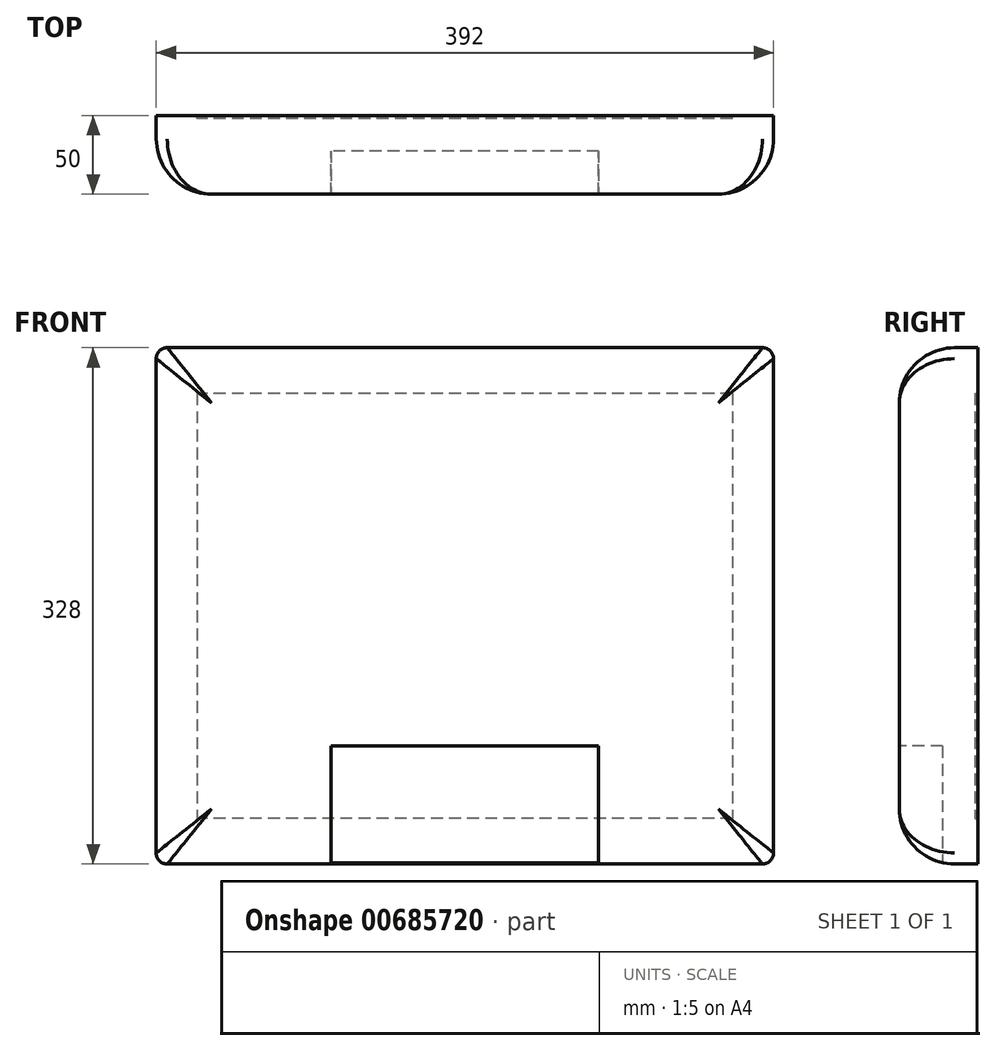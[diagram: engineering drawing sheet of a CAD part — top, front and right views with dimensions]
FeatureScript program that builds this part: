
annotation { "Feature Type Name" : "Feature", "Feature Type Description" : "" }
export const myFeature = defineFeature(function(context is Context, id is Id, definition is map)
    precondition{}
    {
        {
            var Q0;
            Q0=qCreatedBy(makeId("Front.planeOp"),FACE);
            var sketch = newSketch(context, id + "F0", { "sketchPlane" : qUnion([Q0])});
            skLineSegment(sketch, "E0.bottom", {"start": v(189, 164) * mm, "end": v(-189, 164) * mm});
            skLineSegment(sketch, "E0.top", {"start": v(189, -164) * mm, "end": v(-189, -164) * mm});
            skLineSegment(sketch, "E0.left", {"start": v(196, 157) * mm, "end": v(196, -157) * mm});
            skLineSegment(sketch, "E0.right", {"start": v(-196, 157) * mm, "end": v(-196, -157) * mm});
            skPoint(sketch, "E0.middle", {"position": v(0, 0) * mm});
            skPoint(sketch, "E1.visualSharp", {"position": v(-196, 164) * mm});
            skArc(sketch, "E1.filletArc", {"start": v(-189, 164) * mm, "mid": v(-193.95, 161.95) * mm, "end": v(-196, 157) * mm});
            skPoint(sketch, "E2.visualSharp", {"position": v(196, 164) * mm});
            skArc(sketch, "E2.filletArc", {"start": v(196, 157) * mm, "mid": v(193.95, 161.95) * mm, "end": v(189, 164) * mm});
            skPoint(sketch, "E3.visualSharp", {"position": v(196, -164) * mm});
            skArc(sketch, "E3.filletArc", {"start": v(189, -164) * mm, "mid": v(193.95, -161.95) * mm, "end": v(196, -157) * mm});
            skPoint(sketch, "E4.visualSharp", {"position": v(-196, -164) * mm});
            skArc(sketch, "E4.filletArc", {"start": v(-196, -157) * mm, "mid": v(-193.95, -161.95) * mm, "end": v(-189, -164) * mm});
            skSolve(sketch);
        }
        {
            var Q0;
            Q0=makeQuery(id+"F0.imprint","IMPRINT",FACE,{"disambiguationData":[TD([[makeQuery(id+"F0.imprint","IMPRINT",EDGE,{"derivedFrom":sQuery(id+"F0.wireOp",EDGE,"E0.bottom")}),1.0]])]});
            extrude(context, id + "F1", {"entities" : qUnion([Q0]), "depth" : 50 * mm, "offsetDistance" : 25 * mm});
        }
        {
            var Q0;
            Q0=makeQuery(id+"F1.opExtrude","CAP_FACE",FACE,{"disambiguationData":[OSD([sQuery(id+"F0.wireOp",EDGE,"E0.bottom"),sQuery(id+"F0.wireOp",EDGE,"E0.top"),sQuery(id+"F0.wireOp",EDGE,"E0.left"),sQuery(id+"F0.wireOp",EDGE,"E0.right"),sQuery(id+"F0.wireOp",EDGE,"E1.filletArc"),sQuery(id+"F0.wireOp",EDGE,"E2.filletArc"),sQuery(id+"F0.wireOp",EDGE,"E3.filletArc"),sQuery(id+"F0.wireOp",EDGE,"E4.filletArc")])],"isStart":false});
            fillet(context, id + "F2", {"entities" : qUnion([Q0]), "radius" : 35 * mm, "tangentPropagation" : true, "allowEdgeOverflow" : false});
        }
        {
            var Q0;
            Q0=makeQuery(id+"F1.opExtrude","CAP_FACE",FACE,{"disambiguationData":[OSD([sQuery(id+"F0.wireOp",EDGE,"E0.bottom"),sQuery(id+"F0.wireOp",EDGE,"E0.top"),sQuery(id+"F0.wireOp",EDGE,"E0.left"),sQuery(id+"F0.wireOp",EDGE,"E0.right"),sQuery(id+"F0.wireOp",EDGE,"E1.filletArc"),sQuery(id+"F0.wireOp",EDGE,"E2.filletArc"),sQuery(id+"F0.wireOp",EDGE,"E3.filletArc"),sQuery(id+"F0.wireOp",EDGE,"E4.filletArc")])],"isStart":true});
            var sketch = newSketch(context, id + "F3", { "sketchPlane" : qUnion([Q0])});
            skLineSegment(sketch, "E5.bottom", {"start": v(-170, 135) * mm, "end": v(170, 135) * mm});
            skLineSegment(sketch, "E5.top", {"start": v(-170, -135) * mm, "end": v(170, -135) * mm});
            skLineSegment(sketch, "E5.left", {"start": v(-170, 135) * mm, "end": v(-170, -135) * mm});
            skLineSegment(sketch, "E5.right", {"start": v(170, 135) * mm, "end": v(170, -135) * mm});
            skPoint(sketch, "E5.middle", {"position": v(0, 0) * mm});
            skSolve(sketch);
        }
        {
            var Q0;
            Q0=makeQuery(id+"F3.imprint","IMPRINT",FACE,{"disambiguationData":[TD([[makeQuery(id+"F3.imprint","IMPRINT",EDGE,{"derivedFrom":sQuery(id+"F3.wireOp",EDGE,"E5.bottom")}),-1.0]])]});
            extrude(context, id + "F4", {"entities" : qUnion([Q0]), "operationType" : NewBodyOperationType.REMOVE, "oppositeDirection" : true, "depth" : 2 * mm, "offsetDistance" : 25 * mm});
        }
        {
            var Q0;
            Q0=makeQuery(id+"F1.opExtrude","SWEPT_FACE",FACE,{"disambiguationData":[OSD([sQuery(id+"F0.wireOp",EDGE,"E0.top")])]});
            var sketch = newSketch(context, id + "F5", { "sketchPlane" : qUnion([Q0])});
            skLineSegment(sketch, "E6.bottom", {"start": v(85, 22.59) * mm, "end": v(-85, 22.59) * mm});
            skLineSegment(sketch, "E6.top", {"start": v(85, 78.59) * mm, "end": v(-85, 78.59) * mm});
            skLineSegment(sketch, "E6.left", {"start": v(85, 22.59) * mm, "end": v(85, 78.59) * mm});
            skLineSegment(sketch, "E6.right", {"start": v(-85, 22.59) * mm, "end": v(-85, 78.59) * mm});
            skPoint(sketch, "E6.middle", {"position": v(0, 50.59) * mm});
            skPoint(sketch, "E6.middle.positionSnap0", {"position": v(0, 15) * mm});
            skPoint(sketch, "E6.centerSnap0", {"position": v(0, 15) * mm});
            skSolve(sketch);
        }
        {
            var Q0;
            Q0=makeQuery(id+"F5.imprint","IMPRINT",FACE,{"disambiguationData":[TD([[makeQuery(id+"F5.imprint","IMPRINT",EDGE,{"derivedFrom":sQuery(id+"F5.wireOp",EDGE,"E6.bottom")}),-1.0]])]});
            extrude(context, id + "F6", {"entities" : qUnion([Q0]), "operationType" : NewBodyOperationType.REMOVE, "oppositeDirection" : true, "depth" : 75 * mm, "offsetDistance" : 25 * mm});
        }
    });
